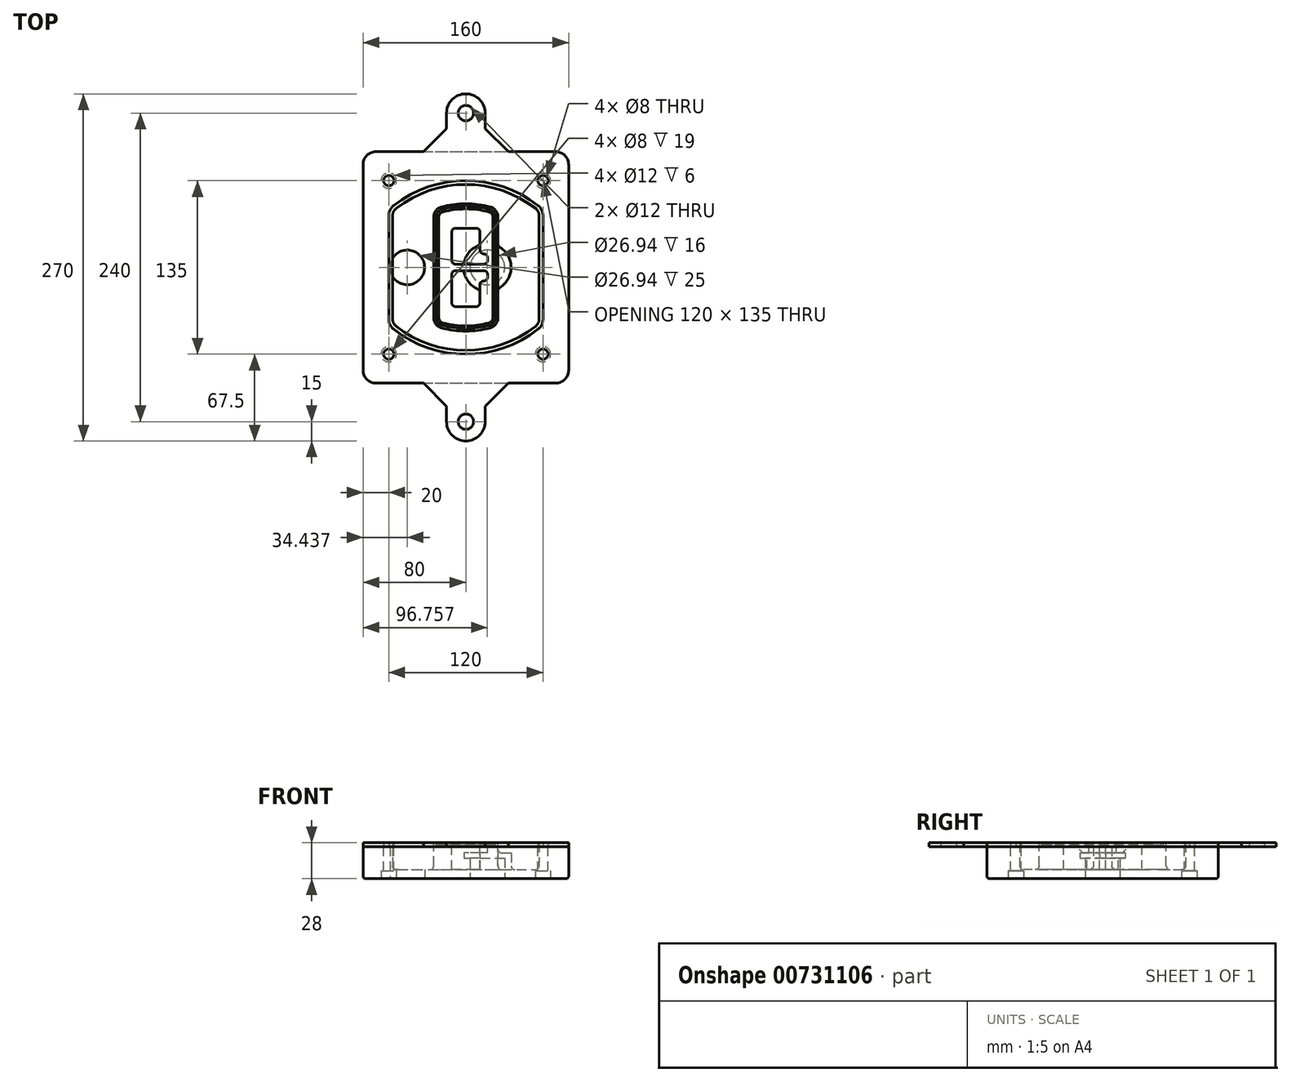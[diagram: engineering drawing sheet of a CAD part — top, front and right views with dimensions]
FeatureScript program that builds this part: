
annotation { "Feature Type Name" : "Feature", "Feature Type Description" : "" }
export const myFeature = defineFeature(function(context is Context, id is Id, definition is map)
    precondition{}
    {
        {
            var Q0;
            Q0=qCreatedBy(makeId("Top.planeOp"),FACE);
            var sketch = newSketch(context, id + "F0", { "sketchPlane" : qUnion([Q0])});
            skPoint(sketch, "E0.rect.middle", {"position": v(0, 0) * mm});
            skLineSegment(sketch, "E1.bottom", {"start": v(-70, -90) * mm, "end": v(70, -90) * mm});
            skLineSegment(sketch, "E1.top", {"start": v(-70, 90) * mm, "end": v(70, 90) * mm});
            skLineSegment(sketch, "E1.left", {"start": v(-80, -80) * mm, "end": v(-80, 80) * mm});
            skLineSegment(sketch, "E1.right", {"start": v(80, -80) * mm, "end": v(80, 80) * mm});
            skLineSegment(sketch, "E2", {"start": v(-80, 90) * mm, "end": v(80, -90) * mm, "construction": true});
            skLineSegment(sketch, "E3", {"start": v(80, 90) * mm, "end": v(-80, -90) * mm, "construction": true});
            skCircle(sketch, "E4", {"center": v(-60, 67.5) * mm, "radius": 4 * mm});
            skCircle(sketch, "E5", {"center": v(60, 67.5) * mm, "radius": 4 * mm});
            skCircle(sketch, "E6", {"center": v(60, -67.5) * mm, "radius": 4 * mm});
            skCircle(sketch, "E7", {"center": v(-60, -67.5) * mm, "radius": 4 * mm});
            skLineSegment(sketch, "E8", {"start": v(-60, 67.5) * mm, "end": v(60, 67.5) * mm, "construction": true});
            skLineSegment(sketch, "E9", {"start": v(60, 67.5) * mm, "end": v(60, -67.5) * mm, "construction": true});
            skLineSegment(sketch, "E10", {"start": v(60, -67.5) * mm, "end": v(-60, -67.5) * mm, "construction": true});
            skLineSegment(sketch, "E11", {"start": v(-60, -67.5) * mm, "end": v(-60, 67.5) * mm, "construction": true});
            skLineSegment(sketch, "E12", {"start": v(-60, 40.3) * mm, "end": v(-60, -40.3) * mm});
            skLineSegment(sketch, "E13", {"start": v(60, 40.3) * mm, "end": v(60, -40.3) * mm});
            skArc(sketch, "E14", {"start": v(56.15, 48.18) * mm, "mid": v(0, 67.5) * mm, "end": v(-56.15, 48.18) * mm});
            skArc(sketch, "E15", {"start": v(-56.15, -48.18) * mm, "mid": v(0, -67.5) * mm, "end": v(56.15, -48.18) * mm});
            skLineSegment(sketch, "E16", {"start": v(-60, 0) * mm, "end": v(60, 0) * mm, "construction": true});
            skPoint(sketch, "E17.visualSharp", {"position": v(-60, -45) * mm});
            skArc(sketch, "E17.filletArc", {"start": v(-60, -40.3) * mm, "mid": v(-58.99, -44.68) * mm, "end": v(-56.15, -48.18) * mm});
            skPoint(sketch, "E18.visualSharp", {"position": v(-60, 45) * mm});
            skArc(sketch, "E18.filletArc", {"start": v(-56.15, 48.18) * mm, "mid": v(-58.99, 44.68) * mm, "end": v(-60, 40.3) * mm});
            skPoint(sketch, "E19.visualSharp", {"position": v(60, 45) * mm});
            skArc(sketch, "E19.filletArc", {"start": v(60, 40.3) * mm, "mid": v(58.99, 44.68) * mm, "end": v(56.15, 48.18) * mm});
            skPoint(sketch, "E20.visualSharp", {"position": v(60, -45) * mm});
            skArc(sketch, "E20.filletArc", {"start": v(56.15, -48.18) * mm, "mid": v(58.99, -44.68) * mm, "end": v(60, -40.3) * mm});
            skPoint(sketch, "E21.visualSharp", {"position": v(-80, 90) * mm});
            skArc(sketch, "E21.filletArc", {"start": v(-70, 90) * mm, "mid": v(-77.07, 87.07) * mm, "end": v(-80, 80) * mm});
            skPoint(sketch, "E22.visualSharp", {"position": v(80, 90) * mm});
            skArc(sketch, "E22.filletArc", {"start": v(80, 80) * mm, "mid": v(77.07, 87.07) * mm, "end": v(70, 90) * mm});
            skPoint(sketch, "E23.visualSharp", {"position": v(80, -90) * mm});
            skArc(sketch, "E23.filletArc", {"start": v(70, -90) * mm, "mid": v(77.07, -87.07) * mm, "end": v(80, -80) * mm});
            skPoint(sketch, "E24.visualSharp", {"position": v(-80, -90) * mm});
            skArc(sketch, "E24.filletArc", {"start": v(-80, -80) * mm, "mid": v(-77.07, -87.07) * mm, "end": v(-70, -90) * mm});
            skArc(sketch, "E25.0", {"start": v(57, 40.3) * mm, "mid": v(56.3, 43.36) * mm, "end": v(54.3, 45.81) * mm});
            skLineSegment(sketch, "E25.1", {"start": v(57, 40.3) * mm, "end": v(57, -40.3) * mm});
            skArc(sketch, "E25.2", {"start": v(54.3, -45.81) * mm, "mid": v(56.3, -43.36) * mm, "end": v(57, -40.3) * mm});
            skArc(sketch, "E25.3", {"start": v(-54.3, -45.81) * mm, "mid": v(0, -64.5) * mm, "end": v(54.3, -45.81) * mm});
            skArc(sketch, "E25.4", {"start": v(-57, -40.3) * mm, "mid": v(-56.3, -43.36) * mm, "end": v(-54.3, -45.81) * mm});
            skArc(sketch, "E25.5", {"start": v(54.3, 45.81) * mm, "mid": v(0, 64.5) * mm, "end": v(-54.3, 45.81) * mm});
            skLineSegment(sketch, "E25.6", {"start": v(-57, 40.3) * mm, "end": v(-57, -40.3) * mm});
            skArc(sketch, "E25.7", {"start": v(-54.3, 45.81) * mm, "mid": v(-56.3, 43.36) * mm, "end": v(-57, 40.3) * mm});
            skArc(sketch, "E26.0", {"start": v(-58.62, 51.33) * mm, "mid": v(-62.58, 46.43) * mm, "end": v(-64, 40.3) * mm});
            skArc(sketch, "E26.1", {"start": v(58.62, 51.33) * mm, "mid": v(0, 71.5) * mm, "end": v(-58.62, 51.33) * mm});
            skArc(sketch, "E26.2", {"start": v(64, 40.3) * mm, "mid": v(62.58, 46.43) * mm, "end": v(58.62, 51.33) * mm});
            skLineSegment(sketch, "E26.3", {"start": v(64, 40.3) * mm, "end": v(64, -40.3) * mm});
            skArc(sketch, "E26.4", {"start": v(58.62, -51.33) * mm, "mid": v(62.58, -46.43) * mm, "end": v(64, -40.3) * mm});
            skLineSegment(sketch, "E26.5", {"start": v(-64, 40.3) * mm, "end": v(-64, -40.3) * mm});
            skArc(sketch, "E26.6", {"start": v(-58.62, -51.33) * mm, "mid": v(0, -71.5) * mm, "end": v(58.62, -51.33) * mm});
            skArc(sketch, "E26.7", {"start": v(-64, -40.3) * mm, "mid": v(-62.58, -46.43) * mm, "end": v(-58.62, -51.33) * mm});
            skSolve(sketch);
        }
        {
            var Q0;
            Q0=makeQuery(id+"F0.imprint","IMPRINT",FACE,{"disambiguationData":[TD([[makeQuery(id+"F0.imprint","IMPRINT",EDGE,{"derivedFrom":sQuery(id+"F0.wireOp",EDGE,"E1.bottom")}),1.0]])]});
            var Q1;
            Q1=makeQuery(id+"F0.imprint","IMPRINT",FACE,{"disambiguationData":[TD([[makeQuery(id+"F0.imprint","IMPRINT",EDGE,{"derivedFrom":sQuery(id+"F0.wireOp",EDGE,"E12")}),1.0]])]});
            var Q2;
            Q2=makeQuery(id+"F0.imprint","IMPRINT",FACE,{"disambiguationData":[TD([[makeQuery(id+"F0.imprint","IMPRINT",EDGE,{"derivedFrom":sQuery(id+"F0.wireOp",EDGE,"E25.0")}),1.0]])]});
            var Q3;
            Q3=makeQuery(id+"F0.imprint","IMPRINT",FACE,{"disambiguationData":[TD([[makeQuery(id+"F0.imprint","IMPRINT",EDGE,{"derivedFrom":sQuery(id+"F0.wireOp",EDGE,"E12")}),-1.0]])]});
            extrude(context, id + "F1", {"entities" : qUnion([Q0, Q1, Q2, Q3]), "oppositeDirection" : true, "depth" : 25 * mm});
        }
        {
            var Q0;
            Q0=makeQuery(id+"F0.imprint","IMPRINT",FACE,{"disambiguationData":[TD([[makeQuery(id+"F0.imprint","IMPRINT",EDGE,{"derivedFrom":sQuery(id+"F0.wireOp",EDGE,"E12")}),1.0]])]});
            extrude(context, id + "F2", {"entities" : qUnion([Q0]), "operationType" : NewBodyOperationType.ADD, "depth" : 3 * mm});
        }
        {
            var Q0;
            Q0=makeQuery(id+"F0.imprint","IMPRINT",FACE,{"disambiguationData":[TD([[makeQuery(id+"F0.imprint","IMPRINT",EDGE,{"derivedFrom":sQuery(id+"F0.wireOp",EDGE,"E25.0")}),1.0]])]});
            extrude(context, id + "F3", {"entities" : qUnion([Q0]), "operationType" : NewBodyOperationType.REMOVE, "oppositeDirection" : true, "depth" : 18 * mm});
        }
        {
            var Q0;
            Q0=makeQuery(id+"F2.opExtrude","CAP_FACE",FACE,{"disambiguationData":[OSD([sQuery(id+"F0.wireOp",EDGE,"E12"),sQuery(id+"F0.wireOp",EDGE,"E13"),sQuery(id+"F0.wireOp",EDGE,"E14"),sQuery(id+"F0.wireOp",EDGE,"E15"),sQuery(id+"F0.wireOp",EDGE,"E17.filletArc"),sQuery(id+"F0.wireOp",EDGE,"E18.filletArc"),sQuery(id+"F0.wireOp",EDGE,"E19.filletArc"),sQuery(id+"F0.wireOp",EDGE,"E20.filletArc"),sQuery(id+"F0.wireOp",EDGE,"E25.0"),sQuery(id+"F0.wireOp",EDGE,"E25.1"),sQuery(id+"F0.wireOp",EDGE,"E25.2"),sQuery(id+"F0.wireOp",EDGE,"E25.3"),sQuery(id+"F0.wireOp",EDGE,"E25.4"),sQuery(id+"F0.wireOp",EDGE,"E25.5"),sQuery(id+"F0.wireOp",EDGE,"E25.6"),sQuery(id+"F0.wireOp",EDGE,"E25.7")])],"isStart":false});
            var sketch = newSketch(context, id + "F4", { "sketchPlane" : qUnion([Q0])});
            skArc(sketch, "E27.0", {"start": v(-19.08, -46.97) * mm, "mid": v(0, -49.5) * mm, "end": v(19.08, -46.97) * mm});
            skArc(sketch, "E28.0", {"start": v(19.08, 46.97) * mm, "mid": v(0, 49.5) * mm, "end": v(-19.08, 46.97) * mm});
            skLineSegment(sketch, "E29", {"start": v(-25, 39.25) * mm, "end": v(-25, -39.25) * mm});
            skLineSegment(sketch, "E30", {"start": v(25, 39.25) * mm, "end": v(25, -39.25) * mm});
            skLineSegment(sketch, "E31", {"start": v(-25, 45.1) * mm, "end": v(25, 45.1) * mm, "construction": true});
            skLineSegment(sketch, "E32", {"start": v(-25, -45.1) * mm, "end": v(25, -45.1) * mm, "construction": true});
            skPoint(sketch, "E33.visualSharp", {"position": v(-25, 45.1) * mm});
            skArc(sketch, "E33.filletArc", {"start": v(-19.08, 46.97) * mm, "mid": v(-23.35, 44.11) * mm, "end": v(-25, 39.25) * mm});
            skPoint(sketch, "E34.visualSharp", {"position": v(25, 45.1) * mm});
            skArc(sketch, "E34.filletArc", {"start": v(25, 39.25) * mm, "mid": v(23.35, 44.11) * mm, "end": v(19.08, 46.97) * mm});
            skPoint(sketch, "E35.visualSharp", {"position": v(25, -45.1) * mm});
            skArc(sketch, "E35.filletArc", {"start": v(19.08, -46.97) * mm, "mid": v(23.35, -44.11) * mm, "end": v(25, -39.25) * mm});
            skPoint(sketch, "E36.visualSharp", {"position": v(-25, -45.1) * mm});
            skArc(sketch, "E36.filletArc", {"start": v(-25, -39.25) * mm, "mid": v(-23.35, -44.11) * mm, "end": v(-19.08, -46.97) * mm});
            skArc(sketch, "E37.0", {"start": v(54.3, 45.81) * mm, "mid": v(0, 64.5) * mm, "end": v(-54.3, 45.81) * mm});
            skArc(sketch, "E37.1", {"start": v(-54.3, 45.81) * mm, "mid": v(-56.3, 43.36) * mm, "end": v(-57, 40.3) * mm});
            skLineSegment(sketch, "E37.2", {"start": v(-57, 40.3) * mm, "end": v(-57, -40.3) * mm});
            skArc(sketch, "E37.3", {"start": v(-57, -40.3) * mm, "mid": v(-56.3, -43.36) * mm, "end": v(-54.3, -45.81) * mm});
            skArc(sketch, "E37.4", {"start": v(-54.3, -45.81) * mm, "mid": v(0, -64.5) * mm, "end": v(54.3, -45.81) * mm});
            skArc(sketch, "E37.5", {"start": v(54.3, -45.81) * mm, "mid": v(56.3, -43.36) * mm, "end": v(57, -40.3) * mm});
            skLineSegment(sketch, "E37.6", {"start": v(57, 40.3) * mm, "end": v(57, -40.3) * mm});
            skArc(sketch, "E37.7", {"start": v(57, 40.3) * mm, "mid": v(56.3, 43.36) * mm, "end": v(54.3, 45.81) * mm});
            skLineSegment(sketch, "E38.0", {"start": v(23, 39.25) * mm, "end": v(23, -39.25) * mm});
            skArc(sketch, "E38.1", {"start": v(18.56, -45.04) * mm, "mid": v(21.76, -42.9) * mm, "end": v(23, -39.25) * mm});
            skArc(sketch, "E38.2", {"start": v(-18.56, -45.04) * mm, "mid": v(0, -47.5) * mm, "end": v(18.56, -45.04) * mm});
            skArc(sketch, "E38.3", {"start": v(-23, -39.25) * mm, "mid": v(-21.76, -42.9) * mm, "end": v(-18.56, -45.04) * mm});
            skLineSegment(sketch, "E38.4", {"start": v(-23, 39.25) * mm, "end": v(-23, -39.25) * mm});
            skArc(sketch, "E38.5", {"start": v(23, 39.25) * mm, "mid": v(21.76, 42.9) * mm, "end": v(18.56, 45.04) * mm});
            skArc(sketch, "E38.6", {"start": v(-18.56, 45.04) * mm, "mid": v(-21.76, 42.9) * mm, "end": v(-23, 39.25) * mm});
            skArc(sketch, "E38.7", {"start": v(18.56, 45.04) * mm, "mid": v(0, 47.5) * mm, "end": v(-18.56, 45.04) * mm});
            skArc(sketch, "E39.0", {"start": v(21, 39.25) * mm, "mid": v(20.18, 41.68) * mm, "end": v(18.04, 43.1) * mm});
            skLineSegment(sketch, "E39.1", {"start": v(21, 39.25) * mm, "end": v(21, -39.25) * mm});
            skArc(sketch, "E39.2", {"start": v(18.04, -43.1) * mm, "mid": v(20.18, -41.68) * mm, "end": v(21, -39.25) * mm});
            skArc(sketch, "E39.3", {"start": v(-18.04, -43.1) * mm, "mid": v(0, -45.5) * mm, "end": v(18.04, -43.1) * mm});
            skArc(sketch, "E39.4", {"start": v(-21, -39.25) * mm, "mid": v(-20.18, -41.68) * mm, "end": v(-18.04, -43.1) * mm});
            skArc(sketch, "E39.5", {"start": v(18.04, 43.1) * mm, "mid": v(0, 45.5) * mm, "end": v(-18.04, 43.1) * mm});
            skLineSegment(sketch, "E39.6", {"start": v(-21, 39.25) * mm, "end": v(-21, -39.25) * mm});
            skArc(sketch, "E39.7", {"start": v(-18.04, 43.1) * mm, "mid": v(-20.18, 41.68) * mm, "end": v(-21, 39.25) * mm});
            skLineSegment(sketch, "E40", {"start": v(-25, 0) * mm, "end": v(25, 0) * mm, "construction": true});
            skLineSegment(sketch, "E41", {"start": v(-11, 5.5) * mm, "end": v(-11, 27.5) * mm});
            skLineSegment(sketch, "E42", {"start": v(-8, 30.5) * mm, "end": v(8, 30.5) * mm});
            skLineSegment(sketch, "E43", {"start": v(11, 27.5) * mm, "end": v(11, 13.5) * mm});
            skLineSegment(sketch, "E44", {"start": v(14, 10.5) * mm, "end": v(14, 10.5) * mm});
            skLineSegment(sketch, "E45", {"start": v(17, 7.5) * mm, "end": v(17, 5.5) * mm});
            skLineSegment(sketch, "E46", {"start": v(14, 2.5) * mm, "end": v(-8, 2.5) * mm});
            skPoint(sketch, "E47.visualSharp", {"position": v(-11, 30.5) * mm});
            skArc(sketch, "E47.filletArc", {"start": v(-8, 30.5) * mm, "mid": v(-10.12, 29.62) * mm, "end": v(-11, 27.5) * mm});
            skPoint(sketch, "E48.visualSharp", {"position": v(11, 30.5) * mm});
            skArc(sketch, "E48.filletArc", {"start": v(11, 27.5) * mm, "mid": v(10.12, 29.62) * mm, "end": v(8, 30.5) * mm});
            skPoint(sketch, "E49.visualSharp", {"position": v(11, 10.5) * mm});
            skArc(sketch, "E49.filletArc", {"start": v(11, 13.5) * mm, "mid": v(11.88, 11.38) * mm, "end": v(14, 10.5) * mm});
            skPoint(sketch, "E50.visualSharp", {"position": v(17, 10.5) * mm});
            skArc(sketch, "E50.filletArc", {"start": v(17, 7.5) * mm, "mid": v(16.12, 9.62) * mm, "end": v(14, 10.5) * mm});
            skPoint(sketch, "E51.visualSharp", {"position": v(17, 2.5) * mm});
            skArc(sketch, "E51.filletArc", {"start": v(14, 2.5) * mm, "mid": v(16.12, 3.38) * mm, "end": v(17, 5.5) * mm});
            skPoint(sketch, "E52.visualSharp", {"position": v(-11, 2.5) * mm});
            skArc(sketch, "E52.filletArc", {"start": v(-11, 5.5) * mm, "mid": v(-10.12, 3.38) * mm, "end": v(-8, 2.5) * mm});
            skLineSegment(sketch, "E53.0.MirrorCS", {"start": v(14, -2.5) * mm, "end": v(-8, -2.5) * mm});
            skArc(sketch, "E54.0.MirrorCS", {"start": v(-11, -5.5) * mm, "mid": v(-10.12, -3.38) * mm, "end": v(-8, -2.5) * mm});
            skLineSegment(sketch, "E55.0.MirrorCS", {"start": v(-11, -5.5) * mm, "end": v(-11, -27.5) * mm});
            skArc(sketch, "E56.0.MirrorCS", {"start": v(-8, -30.5) * mm, "mid": v(-10.12, -29.62) * mm, "end": v(-11, -27.5) * mm});
            skLineSegment(sketch, "E57.0.MirrorCS", {"start": v(-8, -30.5) * mm, "end": v(8, -30.5) * mm});
            skArc(sketch, "E58.0.MirrorCS", {"start": v(11, -27.5) * mm, "mid": v(10.12, -29.62) * mm, "end": v(8, -30.5) * mm});
            skLineSegment(sketch, "E59.0.MirrorCS", {"start": v(11, -27.5) * mm, "end": v(11, -13.5) * mm});
            skArc(sketch, "E60.0.MirrorCS", {"start": v(11, -13.5) * mm, "mid": v(11.88, -11.38) * mm, "end": v(14, -10.5) * mm});
            skArc(sketch, "E61.0.MirrorCS", {"start": v(17, -7.5) * mm, "mid": v(16.12, -9.62) * mm, "end": v(14, -10.5) * mm});
            skLineSegment(sketch, "E62.0.MirrorCS", {"start": v(17, -7.5) * mm, "end": v(17, -5.5) * mm});
            skArc(sketch, "E63.0.MirrorCS", {"start": v(14, -2.5) * mm, "mid": v(16.12, -3.38) * mm, "end": v(17, -5.5) * mm});
            skSolve(sketch);
        }
        {
            var Q0;
            Q0=makeQuery(id+"F4.imprint","IMPRINT",FACE,{"disambiguationData":[TD([[makeQuery(id+"F4.imprint","IMPRINT",EDGE,{"derivedFrom":sQuery(id+"F4.wireOp",EDGE,"E27.0")}),1.0]])]});
            var Q1;
            Q1=makeQuery(id+"F4.imprint","IMPRINT",FACE,{"disambiguationData":[TD([[makeQuery(id+"F4.imprint","IMPRINT",EDGE,{"derivedFrom":sQuery(id+"F4.wireOp",EDGE,"E38.0")}),-1.0]])]});
            var Q2;
            Q2=makeQuery(id+"F4.imprint","IMPRINT",FACE,{"disambiguationData":[TD([[makeQuery(id+"F4.imprint","IMPRINT",EDGE,{"derivedFrom":sQuery(id+"F4.wireOp",EDGE,"E39.0")}),1.0]])]});
            extrude(context, id + "F5", {"entities" : qUnion([Q0, Q1, Q2]), "operationType" : NewBodyOperationType.ADD, "endBound" : BoundingType.UP_TO_NEXT, "oppositeDirection" : true, "depth" : 25 * mm});
        }
        {
            var Q0;
            Q0=makeQuery(id+"F4.imprint","IMPRINT",FACE,{"disambiguationData":[TD([[makeQuery(id+"F4.imprint","IMPRINT",EDGE,{"derivedFrom":sQuery(id+"F4.wireOp",EDGE,"E38.0")}),-1.0]])]});
            extrude(context, id + "F6", {"entities" : qUnion([Q0]), "operationType" : NewBodyOperationType.REMOVE, "oppositeDirection" : true, "depth" : 2 * mm});
        }
        {
            var Q0;
            Q0=makeQuery(id+"F1.opExtrude","CAP_FACE",FACE,{"disambiguationData":[OSD([sQuery(id+"F0.wireOp",EDGE,"E1.bottom"),sQuery(id+"F0.wireOp",EDGE,"E1.top"),sQuery(id+"F0.wireOp",EDGE,"E1.left"),sQuery(id+"F0.wireOp",EDGE,"E1.right"),sQuery(id+"F0.wireOp",EDGE,"E4"),sQuery(id+"F0.wireOp",EDGE,"E5"),sQuery(id+"F0.wireOp",EDGE,"E6"),sQuery(id+"F0.wireOp",EDGE,"E7"),sQuery(id+"F0.wireOp",EDGE,"E21.filletArc"),sQuery(id+"F0.wireOp",EDGE,"E22.filletArc"),sQuery(id+"F0.wireOp",EDGE,"E23.filletArc"),sQuery(id+"F0.wireOp",EDGE,"E24.filletArc")])],"isStart":false});
            var sketch = newSketch(context, id + "F7", { "sketchPlane" : qUnion([Q0])});
            skCircle(sketch, "E64", {"center": v(16.76, 0) * mm, "radius": 13.47 * mm});
            skCircle(sketch, "E65", {"center": v(-45.56, 0) * mm, "radius": 13.47 * mm});
            skLineSegment(sketch, "E66", {"start": v(80, 0) * mm, "end": v(-80, 0) * mm});
            skCircle(sketch, "E67", {"center": v(16.76, 0) * mm, "radius": 18.47 * mm});
            skCircle(sketch, "E68", {"center": v(60, -67.5) * mm, "radius": 6 * mm});
            skCircle(sketch, "E69", {"center": v(-60, -67.5) * mm, "radius": 6 * mm});
            skCircle(sketch, "E70", {"center": v(-60, 67.5) * mm, "radius": 6 * mm});
            skCircle(sketch, "E71", {"center": v(60, 67.5) * mm, "radius": 6 * mm});
            skSolve(sketch);
        }
        {
            var Q0;
            {var subQ1=sQuery(id+"F7.wireOp",EDGE,"E66");var subQ4=sQuery(id+"F7.wireOp",EDGE,"E64");var subQ6=makeQuery(id+"F7.imprint","INTERSECT",VERTEX,{"disambiguationData":[OD(0.0)],"derivedFrom":[subQ4,subQ1]});Q0=makeQuery(id+"F7.imprint","IMPRINT",FACE,{"disambiguationData":[TD([[makeQuery(id+"F7.imprint","IMPRINT",EDGE,{"disambiguationData":[TD([[subQ6,-1.0]])],"derivedFrom":subQ4}),-1.0]])]});}
            var Q1;
            {var subQ0=sQuery(id+"F7.wireOp",EDGE,"E66");var subQ1=sQuery(id+"F7.wireOp",EDGE,"E64");var subQ3=makeQuery(id+"F7.imprint","INTERSECT",VERTEX,{"disambiguationData":[OD(0.0)],"derivedFrom":[subQ1,subQ0]});Q1=makeQuery(id+"F7.imprint","IMPRINT",FACE,{"disambiguationData":[TD([[makeQuery(id+"F7.imprint","IMPRINT",EDGE,{"disambiguationData":[TD([[subQ3,-1.0]])],"derivedFrom":subQ1}),1.0]])]});}
            var Q2;
            {var subQ0=sQuery(id+"F7.wireOp",EDGE,"E66");var subQ1=sQuery(id+"F7.wireOp",EDGE,"E64");var subQ3=makeQuery(id+"F7.imprint","INTERSECT",VERTEX,{"disambiguationData":[OD(0.0)],"derivedFrom":[subQ1,subQ0]});Q2=makeQuery(id+"F7.imprint","IMPRINT",FACE,{"disambiguationData":[TD([[makeQuery(id+"F7.imprint","IMPRINT",EDGE,{"disambiguationData":[TD([[subQ3,1.0]])],"derivedFrom":subQ1}),1.0]])]});}
            var Q3;
            {var subQ1=sQuery(id+"F7.wireOp",EDGE,"E66");var subQ4=sQuery(id+"F7.wireOp",EDGE,"E64");var subQ6=makeQuery(id+"F7.imprint","INTERSECT",VERTEX,{"disambiguationData":[OD(0.0)],"derivedFrom":[subQ4,subQ1]});Q3=makeQuery(id+"F7.imprint","IMPRINT",FACE,{"disambiguationData":[TD([[makeQuery(id+"F7.imprint","IMPRINT",EDGE,{"disambiguationData":[TD([[subQ6,1.0]])],"derivedFrom":subQ4}),-1.0]])]});}
            extrude(context, id + "F8", {"entities" : qUnion([Q0, Q1, Q2, Q3]), "operationType" : NewBodyOperationType.ADD, "oppositeDirection" : true, "depth" : 20 * mm});
        }
        {
            var Q0;
            {var subQ0=sQuery(id+"F7.wireOp",EDGE,"E66");var subQ1=sQuery(id+"F7.wireOp",EDGE,"E64");var subQ3=makeQuery(id+"F7.imprint","INTERSECT",VERTEX,{"disambiguationData":[OD(0.0)],"derivedFrom":[subQ1,subQ0]});Q0=makeQuery(id+"F7.imprint","IMPRINT",FACE,{"disambiguationData":[TD([[makeQuery(id+"F7.imprint","IMPRINT",EDGE,{"disambiguationData":[TD([[subQ3,-1.0]])],"derivedFrom":subQ1}),1.0]])]});}
            var Q1;
            {var subQ0=sQuery(id+"F7.wireOp",EDGE,"E66");var subQ1=sQuery(id+"F7.wireOp",EDGE,"E64");var subQ3=makeQuery(id+"F7.imprint","INTERSECT",VERTEX,{"disambiguationData":[OD(0.0)],"derivedFrom":[subQ1,subQ0]});Q1=makeQuery(id+"F7.imprint","IMPRINT",FACE,{"disambiguationData":[TD([[makeQuery(id+"F7.imprint","IMPRINT",EDGE,{"disambiguationData":[TD([[subQ3,1.0]])],"derivedFrom":subQ1}),1.0]])]});}
            extrude(context, id + "F9", {"entities" : qUnion([Q0, Q1]), "operationType" : NewBodyOperationType.REMOVE, "oppositeDirection" : true, "depth" : 16 * mm});
        }
        {
            var Q0;
            {var subQ0=sQuery(id+"F7.wireOp",EDGE,"E66");var subQ1=sQuery(id+"F7.wireOp",EDGE,"E65");var subQ3=makeQuery(id+"F7.imprint","INTERSECT",VERTEX,{"disambiguationData":[OD(0.0)],"derivedFrom":[subQ1,subQ0]});Q0=makeQuery(id+"F7.imprint","IMPRINT",FACE,{"disambiguationData":[TD([[makeQuery(id+"F7.imprint","IMPRINT",EDGE,{"disambiguationData":[TD([[subQ3,-1.0]])],"derivedFrom":subQ1}),1.0]])]});}
            var Q1;
            {var subQ0=sQuery(id+"F7.wireOp",EDGE,"E66");var subQ1=sQuery(id+"F7.wireOp",EDGE,"E65");var subQ3=makeQuery(id+"F7.imprint","INTERSECT",VERTEX,{"disambiguationData":[OD(0.0)],"derivedFrom":[subQ1,subQ0]});Q1=makeQuery(id+"F7.imprint","IMPRINT",FACE,{"disambiguationData":[TD([[makeQuery(id+"F7.imprint","IMPRINT",EDGE,{"disambiguationData":[TD([[subQ3,1.0]])],"derivedFrom":subQ1}),1.0]])]});}
            extrude(context, id + "F10", {"entities" : qUnion([Q0, Q1]), "operationType" : NewBodyOperationType.REMOVE, "oppositeDirection" : true, "depth" : 25 * mm});
        }
        {
            var Q0;
            Q0=makeQuery(id+"F7.imprint","IMPRINT",FACE,{"disambiguationData":[TD([[makeQuery(id+"F7.imprint","IMPRINT",EDGE,{"derivedFrom":sQuery(id+"F7.wireOp",EDGE,"E68")}),1.0]])]});
            var Q1;
            Q1=makeQuery(id+"F7.imprint","IMPRINT",FACE,{"disambiguationData":[TD([[makeQuery(id+"F7.imprint","IMPRINT",EDGE,{"derivedFrom":makeQuery(id+"F1.opExtrude","CAP_EDGE",EDGE,{"disambiguationData":[OSD([sQuery(id+"F0.wireOp",EDGE,"E5")])],"isStart":false})}),-1.0]])]});
            var Q2;
            Q2=makeQuery(id+"F7.imprint","IMPRINT",FACE,{"disambiguationData":[TD([[makeQuery(id+"F7.imprint","IMPRINT",EDGE,{"derivedFrom":sQuery(id+"F7.wireOp",EDGE,"E69")}),1.0]])]});
            var Q3;
            Q3=makeQuery(id+"F7.imprint","IMPRINT",FACE,{"disambiguationData":[TD([[makeQuery(id+"F7.imprint","IMPRINT",EDGE,{"derivedFrom":makeQuery(id+"F1.opExtrude","CAP_EDGE",EDGE,{"disambiguationData":[OSD([sQuery(id+"F0.wireOp",EDGE,"E4")])],"isStart":false})}),-1.0]])]});
            var Q4;
            Q4=makeQuery(id+"F7.imprint","IMPRINT",FACE,{"disambiguationData":[TD([[makeQuery(id+"F7.imprint","IMPRINT",EDGE,{"derivedFrom":sQuery(id+"F7.wireOp",EDGE,"E70")}),1.0]])]});
            var Q5;
            Q5=makeQuery(id+"F7.imprint","IMPRINT",FACE,{"disambiguationData":[TD([[makeQuery(id+"F7.imprint","IMPRINT",EDGE,{"derivedFrom":makeQuery(id+"F1.opExtrude","CAP_EDGE",EDGE,{"disambiguationData":[OSD([sQuery(id+"F0.wireOp",EDGE,"E7")])],"isStart":false})}),-1.0]])]});
            var Q6;
            Q6=makeQuery(id+"F7.imprint","IMPRINT",FACE,{"disambiguationData":[TD([[makeQuery(id+"F7.imprint","IMPRINT",EDGE,{"derivedFrom":sQuery(id+"F7.wireOp",EDGE,"E71")}),1.0]])]});
            var Q7;
            Q7=makeQuery(id+"F7.imprint","IMPRINT",FACE,{"disambiguationData":[TD([[makeQuery(id+"F7.imprint","IMPRINT",EDGE,{"derivedFrom":makeQuery(id+"F1.opExtrude","CAP_EDGE",EDGE,{"disambiguationData":[OSD([sQuery(id+"F0.wireOp",EDGE,"E6")])],"isStart":false})}),-1.0]])]});
            extrude(context, id + "F11", {"entities" : qUnion([Q0, Q1, Q2, Q3, Q4, Q5, Q6, Q7]), "operationType" : NewBodyOperationType.REMOVE, "oppositeDirection" : true, "depth" : 6 * mm});
        }
        {
            var Q0;
            Q0=makeQuery(id+"F9.boolean.opBoolean","COPY",FACE,{"derivedFrom":makeQuery(id+"F9.opExtrude","CAP_FACE",FACE,{"disambiguationData":[OSD([sQuery(id+"F7.wireOp",EDGE,"E64")])],"isStart":false})});
            var sketch = newSketch(context, id + "F12", { "sketchPlane" : qUnion([Q0])});
            skArc(sketch, "E72.0", {"start": v(11, 17.55) * mm, "mid": v(2.57, 11.82) * mm, "end": v(-1.54, 2.5) * mm});
            skArc(sketch, "E72.1", {"start": v(-1.54, -2.5) * mm, "mid": v(2.57, -11.82) * mm, "end": v(11, -17.55) * mm});
            skLineSegment(sketch, "E73", {"start": v(-1.54, -2.5) * mm, "end": v(14, -2.5) * mm});
            skLineSegment(sketch, "E74.0", {"start": v(14, 2.5) * mm, "end": v(-1.54, 2.5) * mm});
            skArc(sketch, "E74.1", {"start": v(14, 2.5) * mm, "mid": v(16.12, 3.38) * mm, "end": v(17, 5.5) * mm});
            skLineSegment(sketch, "E74.2", {"start": v(17, 7.5) * mm, "end": v(17, 5.5) * mm});
            skArc(sketch, "E74.3", {"start": v(17, 7.5) * mm, "mid": v(16.12, 9.62) * mm, "end": v(14, 10.5) * mm});
            skArc(sketch, "E74.4", {"start": v(11, 13.5) * mm, "mid": v(11.88, 11.38) * mm, "end": v(14, 10.5) * mm});
            skLineSegment(sketch, "E74.5", {"start": v(11, 17.55) * mm, "end": v(11, 13.5) * mm});
            skLineSegment(sketch, "E74.7", {"start": v(14, -2.5) * mm, "end": v(-1.54, -2.5) * mm});
            skArc(sketch, "E74.8", {"start": v(14, -2.5) * mm, "mid": v(16.12, -3.38) * mm, "end": v(17, -5.5) * mm});
            skLineSegment(sketch, "E74.9", {"start": v(17, -7.5) * mm, "end": v(17, -5.5) * mm});
            skArc(sketch, "E74.10", {"start": v(17, -7.5) * mm, "mid": v(16.12, -9.62) * mm, "end": v(14, -10.5) * mm});
            skArc(sketch, "E74.11", {"start": v(11, -13.5) * mm, "mid": v(11.88, -11.38) * mm, "end": v(14, -10.5) * mm});
            skLineSegment(sketch, "E74.12", {"start": v(11, -17.55) * mm, "end": v(11, -13.5) * mm});
            skPoint(sketch, "E75.orphan", {"position": v(11, -27.5) * mm});
            skPoint(sketch, "E76.orphan", {"position": v(-8, -2.5) * mm});
            skPoint(sketch, "E77.orphan", {"position": v(-8, 2.5) * mm});
            skPoint(sketch, "E78.orphan", {"position": v(11, 27.5) * mm});
            skSolve(sketch);
        }
        {
            var Q0;
            {var subQ7=sQuery(id+"F12.wireOp",EDGE,"E72.0");var subQ14=sQuery(id+"F12.wireOp",EDGE,"E72.1");var subQ16=sQuery(id+"F12.wireOp",EDGE,"E74.1");var subQ18=sQuery(id+"F12.wireOp",EDGE,"E74.8");Q0=qUnion([makeQuery(id+"F12.imprint","IMPRINT",FACE,{"disambiguationData":[TD([[makeQuery(id+"F12.imprint","IMPRINT",EDGE,{"derivedFrom":subQ7}),1.0]])]}),makeQuery(id+"F12.imprint","IMPRINT",FACE,{"disambiguationData":[TD([[makeQuery(id+"F12.imprint","IMPRINT",EDGE,{"derivedFrom":subQ14}),1.0]])]}),makeQuery(id+"F12.imprint","IMPRINT",FACE,{"disambiguationData":[TD([[makeQuery(id+"F12.imprint","IMPRINT",EDGE,{"derivedFrom":subQ16}),1.0]])]}),makeQuery(id+"F12.imprint","IMPRINT",FACE,{"disambiguationData":[TD([[makeQuery(id+"F12.imprint","IMPRINT",EDGE,{"derivedFrom":subQ18}),-1.0]])]})]);}
            var Q1;
            Q1=makeQuery(id+"F5.boolean.opBoolean","SPLIT",FACE,{"disambiguationData":[TD([makeQuery(id+"F5.opExtrude","SWEPT_FACE",FACE,{"disambiguationData":[OSD([sQuery(id+"F4.wireOp",EDGE,"E41")])]})])],"derivedFrom":makeQuery(id+"F3.boolean.opBoolean","COPY",FACE,{"derivedFrom":makeQuery(id+"F3.opExtrude","CAP_FACE",FACE,{"disambiguationData":[OSD([sQuery(id+"F0.wireOp",EDGE,"E25.0"),sQuery(id+"F0.wireOp",EDGE,"E25.1"),sQuery(id+"F0.wireOp",EDGE,"E25.2"),sQuery(id+"F0.wireOp",EDGE,"E25.3"),sQuery(id+"F0.wireOp",EDGE,"E25.4"),sQuery(id+"F0.wireOp",EDGE,"E25.5"),sQuery(id+"F0.wireOp",EDGE,"E25.6"),sQuery(id+"F0.wireOp",EDGE,"E25.7")])],"isStart":false})})});
            extrude(context, id + "F13", {"entities" : qUnion([Q0]), "operationType" : NewBodyOperationType.REMOVE, "endBound" : BoundingType.UP_TO_SURFACE, "endBoundEntityFace" : qUnion([Q1]), "depth" : 25 * mm});
        }
        {
            var Q0;
            Q0=makeQuery(id+"F3.boolean.opBoolean","COPY",EDGE,{"derivedFrom":makeQuery(id+"F3.opExtrude","CAP_EDGE",EDGE,{"disambiguationData":[OSD([sQuery(id+"F0.wireOp",EDGE,"E25.6")])],"isStart":false})});
            var Q1;
            Q1=makeQuery(id+"F8.boolean.opBoolean","INTERSECT",EDGE,{"derivedFrom":[makeQuery(id+"F5.opExtrude","SWEPT_FACE",FACE,{"disambiguationData":[OSD([sQuery(id+"F4.wireOp",EDGE,"E30")])]}),makeQuery(id+"F8.opExtrude","CAP_FACE",FACE,{"disambiguationData":[OSD([sQuery(id+"F7.wireOp",EDGE,"E67")])],"isStart":false})]});
            var Q2;
            Q2=makeQuery(id+"F8.boolean.opBoolean","INTERSECT",EDGE,{"disambiguationData":[OD(1.0)],"derivedFrom":[makeQuery(id+"F5.opExtrude","SWEPT_FACE",FACE,{"disambiguationData":[OSD([sQuery(id+"F4.wireOp",EDGE,"E30")])]}),makeQuery(id+"F8.opExtrude","SWEPT_FACE",FACE,{"disambiguationData":[OSD([sQuery(id+"F7.wireOp",EDGE,"E67")])]})]});
            var Q3;
            {var subQ0=sQuery(id+"F4.wireOp",EDGE,"E30");Q3=makeQuery(id+"F8.boolean.opBoolean","SPLIT",EDGE,{"disambiguationData":[TD([makeQuery(id+"F5.opExtrude","SWEPT_FACE",FACE,{"disambiguationData":[OSD([sQuery(id+"F4.wireOp",EDGE,"E35.filletArc")])]})])],"derivedFrom":makeQuery(id+"F5.opExtrude","CAP_EDGE",EDGE,{"disambiguationData":[OSD([subQ0])],"isStart":false})});}
            var Q4;
            {var subQ0=sQuery(id+"F0.wireOp",EDGE,"E25.7");var subQ1=sQuery(id+"F0.wireOp",EDGE,"E25.1");var subQ2=sQuery(id+"F0.wireOp",EDGE,"E25.6");var subQ3=sQuery(id+"F0.wireOp",EDGE,"E25.5");var subQ4=sQuery(id+"F0.wireOp",EDGE,"E25.4");var subQ5=sQuery(id+"F0.wireOp",EDGE,"E25.0");var subQ6=sQuery(id+"F0.wireOp",EDGE,"E25.2");var subQ7=sQuery(id+"F0.wireOp",EDGE,"E25.3");Q4=makeQuery(id+"F8.boolean.opBoolean","INTERSECT",EDGE,{"derivedFrom":[makeQuery(id+"F5.boolean.opBoolean","SPLIT",FACE,{"disambiguationData":[TD([makeQuery(id+"F2.opExtrude","SWEPT_FACE",FACE,{"disambiguationData":[OSD([subQ5])]})])],"derivedFrom":makeQuery(id+"F3.boolean.opBoolean","COPY",FACE,{"derivedFrom":makeQuery(id+"F3.opExtrude","CAP_FACE",FACE,{"disambiguationData":[OSD([subQ5,subQ1,subQ6,subQ7,subQ4,subQ3,subQ2,subQ0])],"isStart":false})})}),makeQuery(id+"F8.opExtrude","SWEPT_FACE",FACE,{"disambiguationData":[OSD([sQuery(id+"F7.wireOp",EDGE,"E67")])]})]});}
            var Q5;
            Q5=makeQuery(id+"F8.boolean.opBoolean","INTERSECT",EDGE,{"disambiguationData":[OD(0.0)],"derivedFrom":[makeQuery(id+"F5.opExtrude","SWEPT_FACE",FACE,{"disambiguationData":[OSD([sQuery(id+"F4.wireOp",EDGE,"E30")])]}),makeQuery(id+"F8.opExtrude","SWEPT_FACE",FACE,{"disambiguationData":[OSD([sQuery(id+"F7.wireOp",EDGE,"E67")])]})]});
            fillet(context, id + "F14", {"entities" : qUnion([Q0, Q1, Q2, Q3, Q4, Q5]), "radius" : 3 * mm, "tangentPropagation" : true, "allowEdgeOverflow" : false});
        }
        {
            var Q0;
            Q0=makeQuery(id+"F1.opExtrude","CAP_EDGE",EDGE,{"disambiguationData":[OSD([sQuery(id+"F0.wireOp",EDGE,"E1.bottom")])],"isStart":false});
            fillet(context, id + "F15", {"entities" : qUnion([Q0]), "radius" : 2 * mm, "tangentPropagation" : true, "allowEdgeOverflow" : false});
        }
        {
            var Q0;
            {var subQ0=sQuery(id+"F0.wireOp",EDGE,"E21.filletArc");var subQ1=sQuery(id+"F0.wireOp",EDGE,"E7");var subQ2=sQuery(id+"F0.wireOp",EDGE,"E6");var subQ3=sQuery(id+"F0.wireOp",EDGE,"E5");var subQ4=sQuery(id+"F0.wireOp",EDGE,"E4");var subQ5=sQuery(id+"F0.wireOp",EDGE,"E22.filletArc");var subQ6=sQuery(id+"F0.wireOp",EDGE,"E1.bottom");var subQ7=sQuery(id+"F0.wireOp",EDGE,"E1.right");var subQ8=sQuery(id+"F0.wireOp",EDGE,"E1.top");var subQ9=sQuery(id+"F0.wireOp",EDGE,"E1.left");var subQ10=sQuery(id+"F0.wireOp",EDGE,"E23.filletArc");var subQ11=sQuery(id+"F0.wireOp",EDGE,"E24.filletArc");Q0=makeQuery(id+"F2.boolean.opBoolean","SPLIT",FACE,{"disambiguationData":[TD([makeQuery(id+"F1.opExtrude","SWEPT_FACE",FACE,{"disambiguationData":[OSD([subQ6])]})])],"derivedFrom":makeQuery(id+"F1.opExtrude","CAP_FACE",FACE,{"disambiguationData":[OSD([subQ6,subQ8,subQ9,subQ7,subQ4,subQ3,subQ2,subQ1,subQ0,subQ5,subQ10,subQ11])],"isStart":true})});}
            var sketch = newSketch(context, id + "F16", { "sketchPlane" : qUnion([Q0])});
            skArc(sketch, "E79.0", {"start": v(56.15, 48.18) * mm, "mid": v(0, 67.5) * mm, "end": v(-56.15, 48.18) * mm});
            skLineSegment(sketch, "E79.1", {"start": v(-60, 40.3) * mm, "end": v(-60, -40.3) * mm});
            skArc(sketch, "E79.2", {"start": v(-56.15, -48.18) * mm, "mid": v(0, -67.5) * mm, "end": v(56.15, -48.18) * mm});
            skLineSegment(sketch, "E79.3", {"start": v(60, 40.3) * mm, "end": v(60, -40.3) * mm});
            skArc(sketch, "E79.4", {"start": v(-56.15, 48.18) * mm, "mid": v(-58.99, 44.68) * mm, "end": v(-60, 40.3) * mm});
            skArc(sketch, "E79.5", {"start": v(-60, -40.3) * mm, "mid": v(-58.99, -44.68) * mm, "end": v(-56.15, -48.18) * mm});
            skArc(sketch, "E79.6", {"start": v(56.15, -48.18) * mm, "mid": v(58.99, -44.68) * mm, "end": v(60, -40.3) * mm});
            skArc(sketch, "E79.7", {"start": v(60, 40.3) * mm, "mid": v(58.99, 44.68) * mm, "end": v(56.15, 48.18) * mm});
            skLineSegment(sketch, "E79.8", {"start": v(-70, 90) * mm, "end": v(70, 90) * mm});
            skArc(sketch, "E79.9", {"start": v(-70, 90) * mm, "mid": v(-77.07, 87.07) * mm, "end": v(-80, 80) * mm});
            skLineSegment(sketch, "E79.10", {"start": v(-80, -80) * mm, "end": v(-80, 80) * mm});
            skLineSegment(sketch, "E79.11", {"start": v(-70, -90) * mm, "end": v(70, -90) * mm});
            skLineSegment(sketch, "E79.12", {"start": v(80, -80) * mm, "end": v(80, 80) * mm});
            skArc(sketch, "E79.13", {"start": v(80, 80) * mm, "mid": v(77.07, 87.07) * mm, "end": v(70, 90) * mm});
            skArc(sketch, "E79.14", {"start": v(70, -90) * mm, "mid": v(77.07, -87.07) * mm, "end": v(80, -80) * mm});
            skArc(sketch, "E79.15", {"start": v(-80, -80) * mm, "mid": v(-77.07, -87.07) * mm, "end": v(-70, -90) * mm});
            skCircle(sketch, "E79.16", {"center": v(-60, -67.5) * mm, "radius": 4 * mm});
            skCircle(sketch, "E79.17", {"center": v(-60, 67.5) * mm, "radius": 4 * mm});
            skCircle(sketch, "E79.18", {"center": v(60, 67.5) * mm, "radius": 4 * mm});
            skCircle(sketch, "E79.19", {"center": v(60, -67.5) * mm, "radius": 4 * mm});
            skLineSegment(sketch, "E80", {"start": v(0, 90) * mm, "end": v(0, 120) * mm, "construction": true});
            skLineSegment(sketch, "E81", {"start": v(-33, 90) * mm, "end": v(-15, 108) * mm});
            skLineSegment(sketch, "E82", {"start": v(-15, 108) * mm, "end": v(-15, 120) * mm});
            skLineSegment(sketch, "E83", {"start": v(33, 90) * mm, "end": v(15, 108) * mm});
            skLineSegment(sketch, "E84", {"start": v(15, 108) * mm, "end": v(15, 120) * mm});
            skArc(sketch, "E85", {"start": v(-15, 120) * mm, "mid": v(0, 135) * mm, "end": v(15, 120) * mm});
            skCircle(sketch, "E86", {"center": v(0, 120) * mm, "radius": 6 * mm});
            skLineSegment(sketch, "E87", {"start": v(-80, 0) * mm, "end": v(80, 0) * mm, "construction": true});
            skLineSegment(sketch, "E88.MirrorCS", {"start": v(-33, -90) * mm, "end": v(-15, -108) * mm});
            skLineSegment(sketch, "E89.MirrorCS", {"start": v(-15, -108) * mm, "end": v(-15, -120) * mm});
            skArc(sketch, "E90.MirrorCS", {"start": v(-15, -120) * mm, "mid": v(0, -135) * mm, "end": v(15, -120) * mm});
            skLineSegment(sketch, "E91.MirrorCS", {"start": v(0, -90) * mm, "end": v(0, -120) * mm, "construction": true});
            skCircle(sketch, "E92.MirrorC", {"center": v(0, -120) * mm, "radius": 6 * mm});
            skLineSegment(sketch, "E93.MirrorCS", {"start": v(15, -108) * mm, "end": v(15, -120) * mm});
            skLineSegment(sketch, "E94.MirrorCS", {"start": v(33, -90) * mm, "end": v(15, -108) * mm});
            skSolve(sketch);
        }
        {
            var Q0;
            Q0 = qSketchRegion(id + "F16", true);
            var Q1;
            Q1=makeQuery(id+"F2.opExtrude","CAP_FACE",FACE,{"disambiguationData":[OSD([sQuery(id+"F0.wireOp",EDGE,"E12"),sQuery(id+"F0.wireOp",EDGE,"E13"),sQuery(id+"F0.wireOp",EDGE,"E14"),sQuery(id+"F0.wireOp",EDGE,"E15"),sQuery(id+"F0.wireOp",EDGE,"E17.filletArc"),sQuery(id+"F0.wireOp",EDGE,"E18.filletArc"),sQuery(id+"F0.wireOp",EDGE,"E19.filletArc"),sQuery(id+"F0.wireOp",EDGE,"E20.filletArc"),sQuery(id+"F0.wireOp",EDGE,"E25.0"),sQuery(id+"F0.wireOp",EDGE,"E25.1"),sQuery(id+"F0.wireOp",EDGE,"E25.2"),sQuery(id+"F0.wireOp",EDGE,"E25.3"),sQuery(id+"F0.wireOp",EDGE,"E25.4"),sQuery(id+"F0.wireOp",EDGE,"E25.5"),sQuery(id+"F0.wireOp",EDGE,"E25.6"),sQuery(id+"F0.wireOp",EDGE,"E25.7")])],"isStart":false});
            extrude(context, id + "F17", {"entities" : qUnion([Q0]), "endBound" : BoundingType.UP_TO_SURFACE, "depth" : 25 * mm, "endBoundEntityFace" : qUnion([Q1]), "offsetDistance" : 25 * mm});
        }
    });
